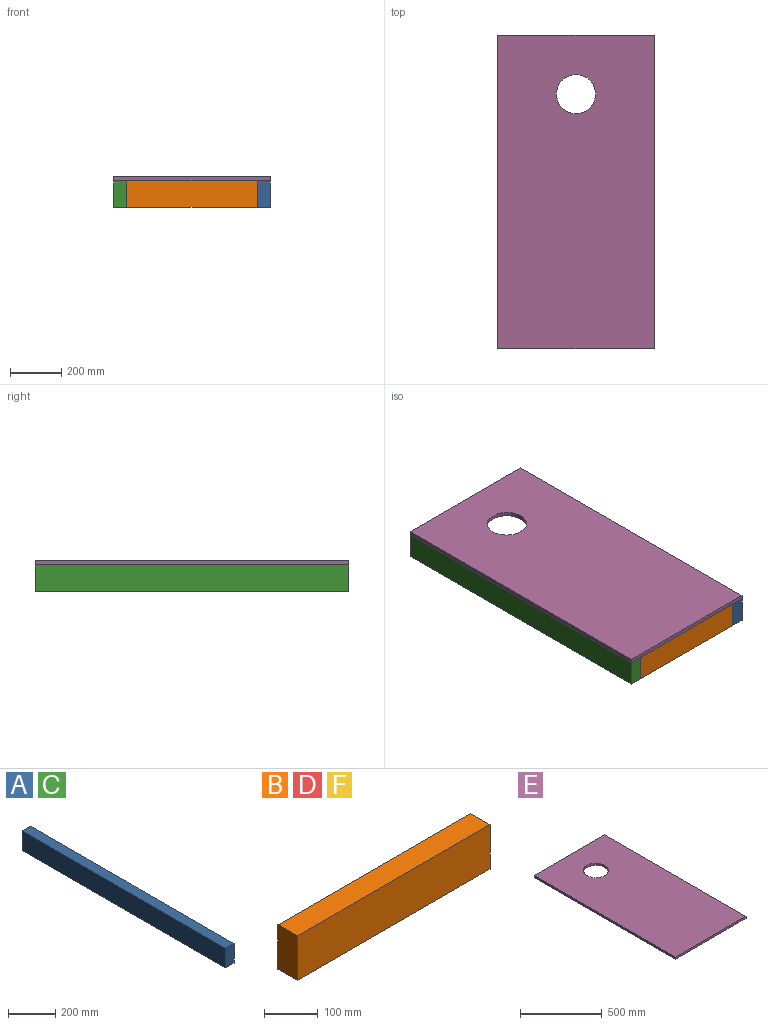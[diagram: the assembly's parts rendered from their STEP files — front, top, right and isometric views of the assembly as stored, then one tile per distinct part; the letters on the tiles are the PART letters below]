
ASSEMBLY  parts=6 mates=5
PART A: 6 faces, bbox 50.8x1219.2x101.6 mm
  f0: plane 1219.2x101.6mm, normal (1,0,0), area 123870.7mm2, adj f1,f3,f4,f5
  f1: plane 1219.2x50.8mm, normal (0,0,1), area 61935.4mm2, adj f0,f2,f4,f5
  f2: plane 1219.2x101.6mm, normal (-1,0,0), area 123870.7mm2, adj f1,f3,f4,f5
  f3: plane 1219.2x50.8mm, normal (0,0,-1), area 61935.4mm2, adj f0,f2,f4,f5
  f4: plane 101.6x50.8mm, normal (0,-1,0), area 5161.3mm2, adj f0,f1,f2,f3
  f5: plane 101.6x50.8mm, normal (0,1,0), area 5161.3mm2, adj f0,f1,f2,f3
PART B: 6 faces, bbox 508x50.8x101.6 mm
  f0: plane 508x101.6mm, normal (0,1,0), area 51612.8mm2, adj f1,f3,f4,f5
  f1: plane 508x50.8mm, normal (0,0,1), area 25806.4mm2, adj f0,f2,f4,f5
  f2: plane 508x101.6mm, normal (0,-1,0), area 51612.8mm2, adj f1,f3,f4,f5
  f3: plane 508x50.8mm, normal (0,0,-1), area 25806.4mm2, adj f0,f2,f4,f5
  f4: plane 101.6x50.8mm, normal (1,0,0), area 5161.3mm2, adj f0,f1,f2,f3
  f5: plane 101.6x50.8mm, normal (-1,0,0), area 5161.3mm2, adj f0,f1,f2,f3
PART C: same geometry as A
PART D: same geometry as B
PART E: 7 faces, bbox 609.6x1219.2x15.9 mm
  f0: plane 1219.2x15.88mm, normal (1,0,0), area 19354.8mm2, adj f1,f4,f5,f6
  f1: plane 609.6x15.88mm, normal (0,1,0), area 9677.4mm2, adj f0,f2,f5,f6
  f2: plane 1219.2x15.88mm, normal (-1,0,0), area 19354.8mm2, adj f1,f4,f5,f6
  f3: cylinder r=76.2mm len=152.4mm, axis (0,0,-1), area 7600.6mm2, adj f5,f6
  f4: plane 609.6x15.88mm, normal (0,-1,0), area 9677.4mm2, adj f0,f2,f5,f6
  f5: plane 1219.2x609.6mm, normal (0,0,1), area 724982.9mm2, adj f0,f1,f2,f3,f4
  f6: plane 1219.2x609.6mm, normal (0,0,-1), area 724982.9mm2, adj f0,f1,f2,f3,f4
PART F: same geometry as B
PLACE A t=(-315.88,247.38,-680.59)mm
PLACE B t=(-849.28,-946.42,-680.59)mm
PLACE C t=(-874.68,247.38,-680.59)mm
PLACE D t=(-849.28,221.98,-680.59)mm
PLACE E t=(-595.28,-362.22,-629.79)mm
PLACE F t=(-849.28,-371.8,-680.59)mm
MATE fastened D.f4 <-> A.f2  axis (1,0,0) through (-341.28,247.38,-731.39)mm
MATE fastened E.f4 <-> A.f4  axis (0,-1,0) through (-290.48,-971.82,-629.79)mm
MATE fastened C.f5 <-> E.f1  axis (0,1,0) through (-900.08,247.38,-629.79)mm
MATE fastened B.f4 <-> A.f2  axis (1,0,0) through (-341.28,-971.82,-731.39)mm
MATE fastened F.f1 <-> E.f6  axis (0,0,1) through (-595.28,-371.8,-629.79)mm
